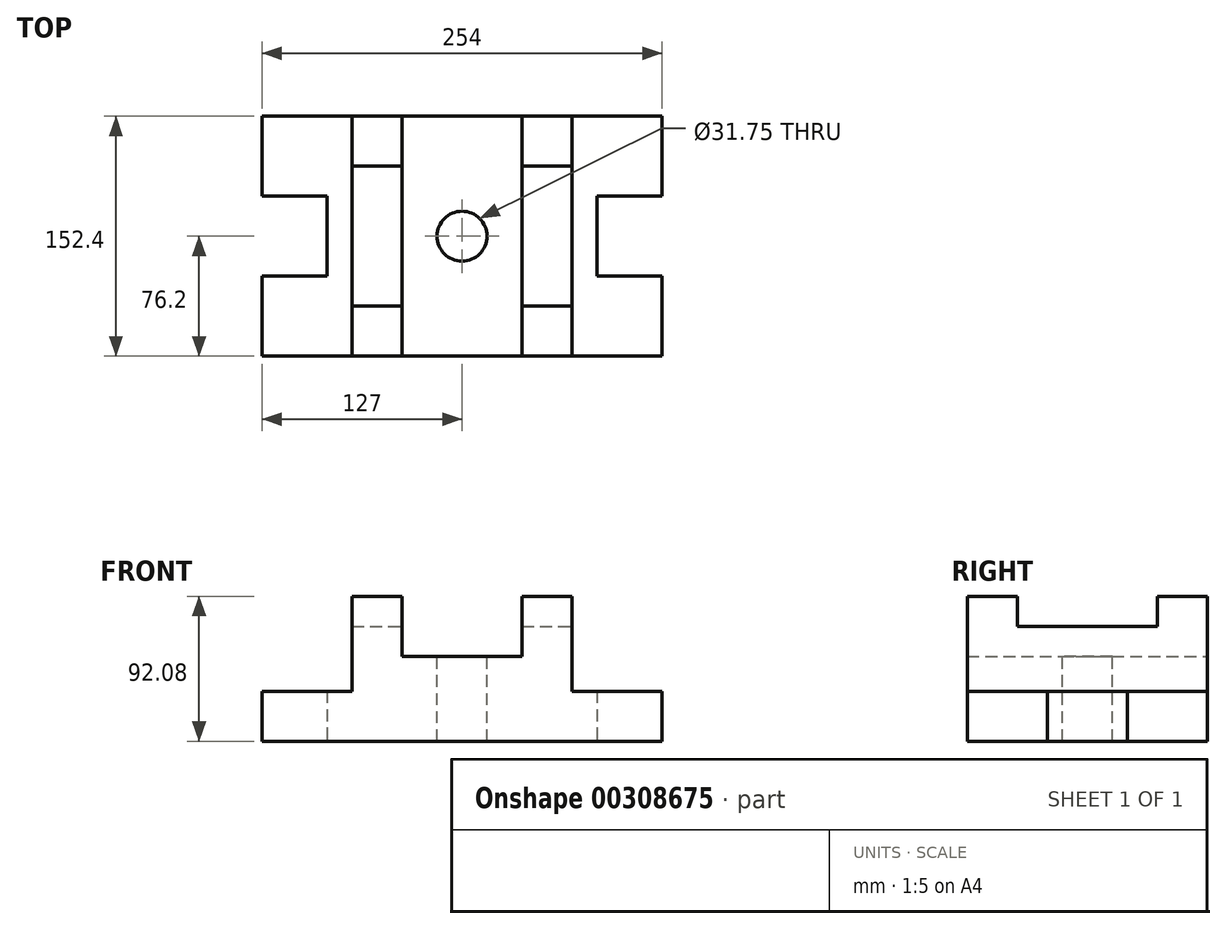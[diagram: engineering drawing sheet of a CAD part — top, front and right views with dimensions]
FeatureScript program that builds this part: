
annotation { "Feature Type Name" : "Feature", "Feature Type Description" : "" }
export const myFeature = defineFeature(function(context is Context, id is Id, definition is map)
    precondition{}
    {
        {
            var Q0;
            Q0=qCreatedBy(makeId("Top.planeOp"),FACE);
            var sketch = newSketch(context, id + "F0", { "sketchPlane" : qUnion([Q0])});
            skPoint(sketch, "E0.middle", {"position": v(0, 0) * mm});
            skLineSegment(sketch, "E1", {"start": v(127, 76.2) * mm, "end": v(69.85, 76.2) * mm});
            skLineSegment(sketch, "E2", {"start": v(-127, 76.2) * mm, "end": v(-69.85, 76.2) * mm});
            skLineSegment(sketch, "E3", {"start": v(127, -76.2) * mm, "end": v(69.85, -76.2) * mm});
            skLineSegment(sketch, "E4.left", {"start": v(-38.1, -44.45) * mm, "end": v(-38.1, -76.2) * mm});
            skLineSegment(sketch, "E5.bottom", {"start": v(-69.85, -44.45) * mm, "end": v(-38.1, -44.45) * mm});
            skLineSegment(sketch, "E5.top", {"start": v(-69.85, 44.45) * mm, "end": v(-38.1, 44.45) * mm});
            skLineSegment(sketch, "E5.right", {"start": v(-38.1, -44.45) * mm, "end": v(-38.1, 44.45) * mm});
            skLineSegment(sketch, "E6.right", {"start": v(-38.1, 44.45) * mm, "end": v(-38.1, 76.2) * mm});
            skLineSegment(sketch, "E7.top", {"start": v(-127, -76.2) * mm, "end": v(-69.85, -76.2) * mm});
            skLineSegment(sketch, "E8", {"start": v(-69.85, 76.2) * mm, "end": v(-69.85, -76.2) * mm});
            skLineSegment(sketch, "E9", {"start": v(69.85, 76.2) * mm, "end": v(38.1, 76.2) * mm});
            skLineSegment(sketch, "E10.bottom", {"start": v(38.1, -44.45) * mm, "end": v(69.85, -44.45) * mm});
            skLineSegment(sketch, "E10.left", {"start": v(38.1, -44.45) * mm, "end": v(38.1, -76.2) * mm});
            skLineSegment(sketch, "E10.right", {"start": v(69.85, -44.45) * mm, "end": v(69.85, -76.2) * mm});
            skLineSegment(sketch, "E11", {"start": v(69.85, -76.2) * mm, "end": v(38.1, -76.2) * mm});
            skLineSegment(sketch, "E12", {"start": v(-38.1, -76.2) * mm, "end": v(38.1, -76.2) * mm});
            skLineSegment(sketch, "E13", {"start": v(69.85, -44.45) * mm, "end": v(69.85, 44.45) * mm});
            skLineSegment(sketch, "E14.top", {"start": v(38.1, 44.45) * mm, "end": v(69.85, 44.45) * mm});
            skLineSegment(sketch, "E14.left", {"start": v(38.1, 76.2) * mm, "end": v(38.1, 44.45) * mm});
            skLineSegment(sketch, "E14.right", {"start": v(69.85, 76.2) * mm, "end": v(69.85, 44.45) * mm});
            skLineSegment(sketch, "E15", {"start": v(38.1, 44.45) * mm, "end": v(38.1, -44.45) * mm});
            skLineSegment(sketch, "E16", {"start": v(38.1, 76.2) * mm, "end": v(-38.1, 76.2) * mm});
            skLineSegment(sketch, "E17", {"start": v(127, -76.2) * mm, "end": v(127, -25.4) * mm});
            skLineSegment(sketch, "E18", {"start": v(127, 76.2) * mm, "end": v(127, 25.4) * mm});
            skLineSegment(sketch, "E19", {"start": v(127, 25.4) * mm, "end": v(85.73, 25.4) * mm});
            skLineSegment(sketch, "E20", {"start": v(85.73, 25.4) * mm, "end": v(85.73, -25.4) * mm});
            skLineSegment(sketch, "E21", {"start": v(85.73, -25.4) * mm, "end": v(127, -25.4) * mm});
            skLineSegment(sketch, "E22", {"start": v(-127, 76.2) * mm, "end": v(-127, 25.4) * mm});
            skLineSegment(sketch, "E23", {"start": v(-127, 25.4) * mm, "end": v(-85.72, 25.4) * mm});
            skLineSegment(sketch, "E24", {"start": v(-85.72, 25.4) * mm, "end": v(-85.72, -25.4) * mm});
            skLineSegment(sketch, "E25", {"start": v(-85.72, -25.4) * mm, "end": v(-127, -25.4) * mm});
            skLineSegment(sketch, "E26", {"start": v(-127, -25.4) * mm, "end": v(-127, -76.2) * mm});
            skLineSegment(sketch, "E27", {"start": v(-69.85, 76.2) * mm, "end": v(-38.1, 76.2) * mm});
            skLineSegment(sketch, "E28", {"start": v(-69.85, -76.2) * mm, "end": v(-38.1, -76.2) * mm});
            skSolve(sketch);
        }
        {
            var Q0;
            Q0=makeQuery(id+"F0.imprint","IMPRINT",FACE,{"disambiguationData":[TD([[makeQuery(id+"F0.imprint","IMPRINT",EDGE,{"derivedFrom":sQuery(id+"F0.wireOp",EDGE,"E4.left")}),1.0]])]});
            extrude(context, id + "F1", {"entities" : qUnion([Q0]), "depth" : 53.97 * mm});
        }
        {
            var Q0;
            {var subQ0=sQuery(id+"F0.wireOp",EDGE,"E5.bottom");Q0=makeQuery(id+"F0.imprint","IMPRINT",FACE,{"disambiguationData":[TD([[makeQuery(id+"F0.imprint","IMPRINT",EDGE,{"derivedFrom":subQ0}),1.0]])]});}
            var Q1;
            Q1=makeQuery(id+"F0.imprint","IMPRINT",FACE,{"disambiguationData":[TD([[makeQuery(id+"F0.imprint","IMPRINT",EDGE,{"derivedFrom":sQuery(id+"F0.wireOp",EDGE,"E10.bottom")}),1.0]])]});
            extrude(context, id + "F2", {"entities" : qUnion([Q0, Q1]), "operationType" : NewBodyOperationType.ADD, "depth" : 73.02 * mm});
        }
        {
            var Q0;
            {var subQ3=sQuery(id+"F0.wireOp",EDGE,"E2");Q0=makeQuery(id+"F0.imprint","IMPRINT",FACE,{"disambiguationData":[TD([[makeQuery(id+"F0.imprint","IMPRINT",EDGE,{"derivedFrom":subQ3}),-1.0]])]});}
            var Q1;
            Q1=makeQuery(id+"F0.imprint","IMPRINT",FACE,{"disambiguationData":[TD([[makeQuery(id+"F0.imprint","IMPRINT",EDGE,{"derivedFrom":sQuery(id+"F0.wireOp",EDGE,"E1")}),1.0]])]});
            extrude(context, id + "F3", {"entities" : qUnion([Q0, Q1]), "operationType" : NewBodyOperationType.ADD, "depth" : 31.75 * mm});
        }
        {
            var Q0;
            Q0=makeQuery(id+"F0.imprint","IMPRINT",FACE,{"disambiguationData":[TD([[makeQuery(id+"F0.imprint","IMPRINT",EDGE,{"derivedFrom":sQuery(id+"F0.wireOp",EDGE,"E10.bottom")}),-1.0]])]});
            var Q1;
            Q1=makeQuery(id+"F0.imprint","IMPRINT",FACE,{"disambiguationData":[TD([[makeQuery(id+"F0.imprint","IMPRINT",EDGE,{"derivedFrom":sQuery(id+"F0.wireOp",EDGE,"E4.left")}),-1.0]])]});
            var Q2;
            Q2=makeQuery(id+"F0.imprint","IMPRINT",FACE,{"disambiguationData":[TD([[makeQuery(id+"F0.imprint","IMPRINT",EDGE,{"derivedFrom":sQuery(id+"F0.wireOp",EDGE,"E9")}),1.0]])]});
            var Q3;
            {var subQ0=sQuery(id+"F0.wireOp",EDGE,"E5.top");Q3=makeQuery(id+"F0.imprint","IMPRINT",FACE,{"disambiguationData":[TD([[makeQuery(id+"F0.imprint","IMPRINT",EDGE,{"derivedFrom":subQ0}),1.0]])]});}
            extrude(context, id + "F4", {"entities" : qUnion([Q0, Q1, Q2, Q3]), "operationType" : NewBodyOperationType.ADD, "depth" : 92.07 * mm});
        }
        {
            var Q0;
            Q0=makeQuery(id+"F1.opExtrude","CAP_FACE",FACE,{"disambiguationData":[OSD([sQuery(id+"F0.wireOp",EDGE,"E4.left"),sQuery(id+"F0.wireOp",EDGE,"E5.right"),sQuery(id+"F0.wireOp",EDGE,"E6.right"),sQuery(id+"F0.wireOp",EDGE,"E10.left"),sQuery(id+"F0.wireOp",EDGE,"E12"),sQuery(id+"F0.wireOp",EDGE,"E14.left"),sQuery(id+"F0.wireOp",EDGE,"E15"),sQuery(id+"F0.wireOp",EDGE,"E16")])],"isStart":false});
            var sketch = newSketch(context, id + "F5", { "sketchPlane" : qUnion([Q0])});
            skCircle(sketch, "E29", {"center": v(0, 0) * mm, "radius": 15.88 * mm});
            skSolve(sketch);
        }
        {
            var Q0;
            Q0=makeQuery(id+"F5.imprint","IMPRINT",FACE,{"disambiguationData":[TD([[makeQuery(id+"F5.imprint","IMPRINT",EDGE,{"derivedFrom":sQuery(id+"F5.wireOp",EDGE,"E29")}),1.0]])]});
            extrude(context, id + "F6", {"entities" : qUnion([Q0]), "operationType" : NewBodyOperationType.REMOVE, "oppositeDirection" : true, "depth" : 53.97 * mm});
        }
    });
